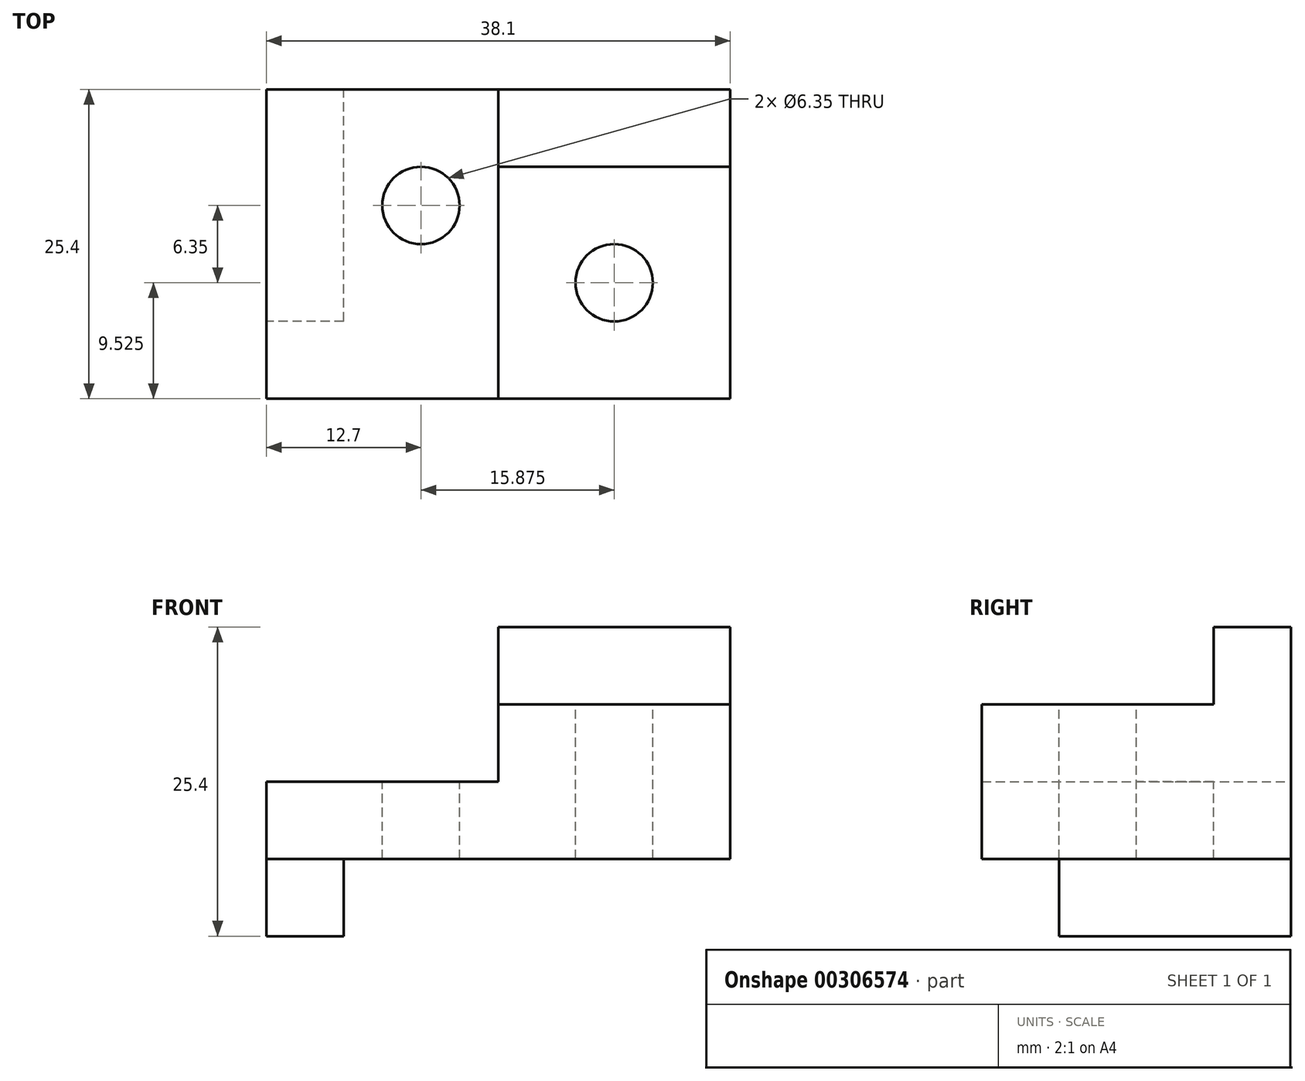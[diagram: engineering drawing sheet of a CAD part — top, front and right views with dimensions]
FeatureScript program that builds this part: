
annotation { "Feature Type Name" : "Feature", "Feature Type Description" : "" }
export const myFeature = defineFeature(function(context is Context, id is Id, definition is map)
    precondition{}
    {
        {
            var Q0;
            Q0=qCreatedBy(makeId("Front.planeOp"),FACE);
            var sketch = newSketch(context, id + "F0", { "sketchPlane" : qUnion([Q0])});
            skLineSegment(sketch, "E0", {"start": v(0, 0) * mm, "end": v(0, 12.7) * mm});
            skLineSegment(sketch, "E1", {"start": v(0, 12.7) * mm, "end": v(19.05, 12.7) * mm});
            skLineSegment(sketch, "E2", {"start": v(19.05, 12.7) * mm, "end": v(19.05, 19.05) * mm});
            skLineSegment(sketch, "E3", {"start": v(19.05, 19.05) * mm, "end": v(38.1, 19.05) * mm});
            skLineSegment(sketch, "E4", {"start": v(38.1, 19.05) * mm, "end": v(38.1, 6.35) * mm});
            skLineSegment(sketch, "E5", {"start": v(38.1, 6.35) * mm, "end": v(6.35, 6.35) * mm});
            skLineSegment(sketch, "E6", {"start": v(6.35, 6.35) * mm, "end": v(6.35, 0) * mm});
            skLineSegment(sketch, "E7", {"start": v(6.35, 0) * mm, "end": v(0, 0) * mm});
            skLineSegment(sketch, "E8", {"start": v(19.05, 19.05) * mm, "end": v(19.05, 25.4) * mm});
            skLineSegment(sketch, "E9", {"start": v(19.05, 25.4) * mm, "end": v(38.1, 25.4) * mm});
            skLineSegment(sketch, "E10", {"start": v(38.1, 25.4) * mm, "end": v(38.1, 19.05) * mm});
            skLineSegment(sketch, "E11", {"start": v(6.35, 6.35) * mm, "end": v(0, 6.35) * mm});
            skSolve(sketch);
        }
        {
            var Q0;
            Q0=makeQuery(id+"F0.imprint","IMPRINT",FACE,{"disambiguationData":[TD([[makeQuery(id+"F0.imprint","IMPRINT",EDGE,{"derivedFrom":sQuery(id+"F0.wireOp",EDGE,"E6")}),-1.0]])]});
            extrude(context, id + "F1", {"entities" : qUnion([Q0]), "depth" : 19.05 * mm});
        }
        {
            var Q0;
            {var subQ0=sQuery(id+"F0.wireOp",EDGE,"E1");Q0=makeQuery(id+"F0.imprint","IMPRINT",FACE,{"disambiguationData":[TD([[makeQuery(id+"F0.imprint","IMPRINT",EDGE,{"derivedFrom":subQ0}),-1.0]])]});}
            extrude(context, id + "F2", {"entities" : qUnion([Q0]), "operationType" : NewBodyOperationType.ADD, "depth" : 25.4 * mm});
        }
        {
            var Q0;
            Q0=makeQuery(id+"F0.imprint","IMPRINT",FACE,{"disambiguationData":[TD([[makeQuery(id+"F0.imprint","IMPRINT",EDGE,{"derivedFrom":sQuery(id+"F0.wireOp",EDGE,"E3")}),1.0]])]});
            extrude(context, id + "F3", {"entities" : qUnion([Q0]), "operationType" : NewBodyOperationType.ADD, "depth" : 6.35 * mm});
        }
        {
            var Q0;
            Q0=makeQuery(id+"F2.opExtrude","SWEPT_FACE",FACE,{"disambiguationData":[OSD([sQuery(id+"F0.wireOp",EDGE,"E1")])]});
            var sketch = newSketch(context, id + "F4", { "sketchPlane" : qUnion([Q0])});
            skCircle(sketch, "E12", {"center": v(12.7, -9.53) * mm, "radius": 3.18 * mm});
            skSolve(sketch);
        }
        {
            var Q0;
            Q0=makeQuery(id+"F4.imprint","IMPRINT",FACE,{"disambiguationData":[TD([[makeQuery(id+"F4.imprint","IMPRINT",EDGE,{"derivedFrom":sQuery(id+"F4.wireOp",EDGE,"E12")}),1.0]])]});
            var Q1;
            Q1=sQuery(id+"F4.wireOp",EDGE,"E12");
            extrude(context, id + "F5", {"entities" : qUnion([Q0]), "operationType" : NewBodyOperationType.REMOVE, "surfaceEntities" : qUnion([Q1]), "oppositeDirection" : true, "depth" : 25.4 * mm});
        }
        {
            var Q0;
            Q0=makeQuery(id+"F2.opExtrude","SWEPT_FACE",FACE,{"disambiguationData":[OSD([sQuery(id+"F0.wireOp",EDGE,"E3")])]});
            var sketch = newSketch(context, id + "F6", { "sketchPlane" : qUnion([Q0])});
            skCircle(sketch, "E13", {"center": v(28.58, -15.88) * mm, "radius": 3.18 * mm});
            skSolve(sketch);
        }
        {
            var Q0;
            Q0=makeQuery(id+"F6.imprint","IMPRINT",FACE,{"disambiguationData":[TD([[makeQuery(id+"F6.imprint","IMPRINT",EDGE,{"derivedFrom":sQuery(id+"F6.wireOp",EDGE,"E13")}),1.0]])]});
            extrude(context, id + "F7", {"entities" : qUnion([Q0]), "operationType" : NewBodyOperationType.REMOVE, "oppositeDirection" : true, "depth" : 25.4 * mm});
        }
    });
